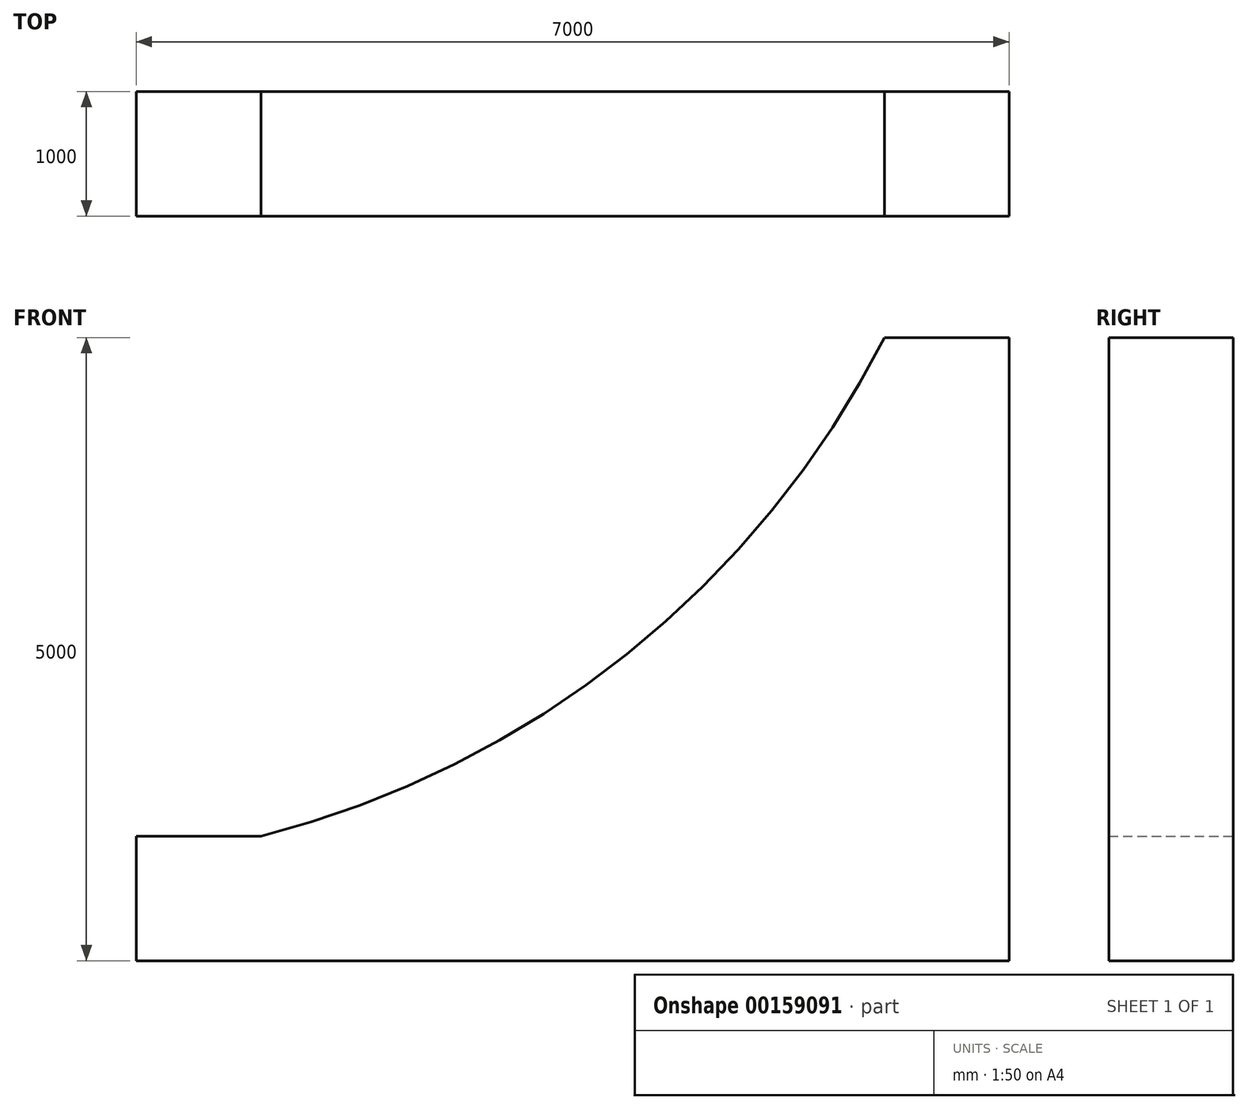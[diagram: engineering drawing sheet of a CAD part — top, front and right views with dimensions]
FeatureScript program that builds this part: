
annotation { "Feature Type Name" : "Feature", "Feature Type Description" : "" }
export const myFeature = defineFeature(function(context is Context, id is Id, definition is map)
    precondition{}
    {
        {
            var Q0;
            Q0=qCreatedBy(makeId("Front.planeOp"),FACE);
            var sketch = newSketch(context, id + "F0", { "sketchPlane" : qUnion([Q0])});
            skLineSegment(sketch, "E0", {"start": v(-1051.48, 0) * mm, "end": v(-51.48, 0) * mm});
            skLineSegment(sketch, "E1", {"start": v(-1051.48, 0) * mm, "end": v(-1051.48, -1000) * mm});
            skLineSegment(sketch, "E2", {"start": v(-1051.48, -1000) * mm, "end": v(5948.52, -1000) * mm});
            skLineSegment(sketch, "E3", {"start": v(5948.52, -1000) * mm, "end": v(5948.52, 4000) * mm});
            skLineSegment(sketch, "E4", {"start": v(5948.52, 4000) * mm, "end": v(4948.52, 4000) * mm});
            skArc(sketch, "E5", {"start": v(-51.48, 0) * mm, "mid": v(2882.1, 1458.02) * mm, "end": v(4948.52, 4000) * mm});
            skSolve(sketch);
        }
        {
            var Q0;
            Q0 = qSketchRegion(id + "F0", true);
            extrude(context, id + "F1", {"entities" : qUnion([Q0]), "depth" : 1000 * mm});
        }
    });
